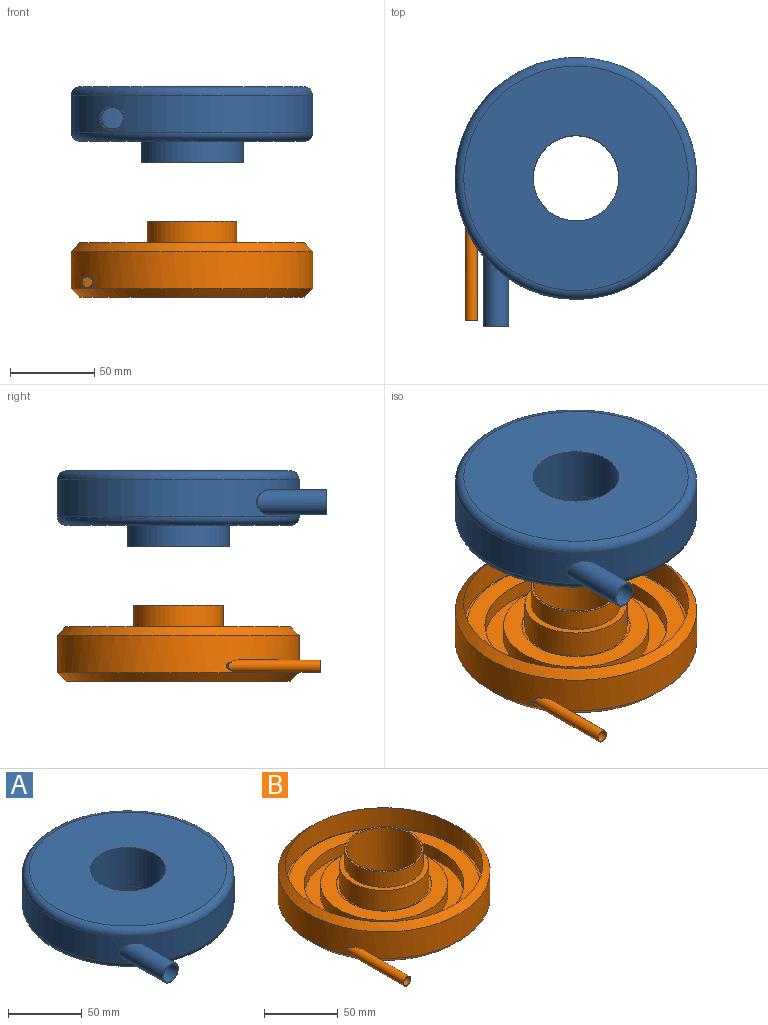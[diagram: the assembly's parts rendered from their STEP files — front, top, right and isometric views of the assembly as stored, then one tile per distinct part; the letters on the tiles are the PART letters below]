
ASSEMBLY  parts=2 mates=1
PART A: 19 faces, bbox 155.5x165.9x45 mm
  f0: cylinder r=71.84mm len=14.01mm, axis (0,0,1), area 32.2mm2, adj f12,f16
  f1: cylinder r=66.86mm len=133.73mm, axis (0,0,1), area 11339.2mm2, adj f9,f11,f12,f13,f14,f15
  f2: cylinder r=30.37mm len=60.74mm, axis (0,0,1), area 7668.5mm2, adj f3,f9
  f3: plane 60.74x60.74mm, normal (0,0,-1), area 665mm2, adj f2,f4
  f4: cylinder r=26.66mm len=53.32mm, axis (0,0,1), area 2127.3mm2, adj f3,f5
  f5: plane 53.32x53.32mm, normal (0,0,-1), area 206mm2, adj f4,f6
  f6: cylinder r=25.4mm len=50.8mm, axis (0,0,1), area 5156.7mm2, adj f5,f7
  f7: plane 133.53x133.53mm, normal (0,0,1), area 11976.3mm2, adj f6,f10
  f8: cylinder r=71.84mm len=143.69mm, axis (0,0,1), area 9765.1mm2, adj f10,f11,f17
  f9: plane 133.73x133.73mm, normal (0,0,-1), area 11148mm2, adj f1,f2
  f10: torus R=66.76mm, axis (0,0,-1), area 3509.5mm2, adj f7,f8
  f11: torus R=66.76mm, axis (0,0,-1), area 3466.8mm2, adj f1,f8
  f12: cylinder r=6.44mm len=19.3mm, axis (0,-1,0), area 280.1mm2, adj f0,f1
  f13: plane 14.95x13.64mm, normal (0,1,0), area 17.6mm2, adj f1,f14,f15
  f14: cylinder r=7.48mm len=14.95mm, axis (0,-1,0), area 316.2mm2, adj f1,f13
  f15: cylinder r=7.01mm len=14.01mm, axis (0,-1,0), area 294.9mm2, adj f1,f13
  f16: cylinder r=7.01mm len=41.12mm, axis (0,-1,0), area 1518mm2, adj f0,f18
  f17: cylinder r=7.48mm len=41.67mm, axis (0,-1,0), area 1622.3mm2, adj f8,f18
  f18: plane 14.95x14.95mm, normal (0,-1,0), area 21.3mm2, adj f16,f17
PART B: 36 faces, bbox 143.7x156.2x45 mm
  f0: plane 60.74x60.74mm, normal (0,0,1), area 665mm2, adj f1,f16
  f1: cylinder r=30.37mm len=60.74mm, axis (0,0,1), area 3205.6mm2, adj f0,f2
  f2: plane 64.4x64.4mm, normal (0,0,1), area 359.5mm2, adj f1,f3
  f3: cylinder r=32.2mm len=64.4mm, axis (0,0,1), area 203.9mm2, adj f2,f4
  f4: plane 86.14x86.14mm, normal (0,0,1), area 2570.7mm2, adj f3,f5
  f5: cylinder r=43.07mm len=86.14mm, axis (0,0,1), area 2605.8mm2, adj f4,f6
  f6: plane 108.33x108.33mm, normal (0,0,1), area 3388.9mm2, adj f5,f7
  f7: cylinder r=54.16mm len=108.33mm, axis (0,0,1), area 3277mm2, adj f6,f8
  f8: plane 130.07x130.07mm, normal (0,0,1), area 4071mm2, adj f7,f9
  f9: cylinder r=65.04mm len=130.07mm, axis (0,0,1), area 411.7mm2, adj f8,f10
  f10: plane 133.73x133.73mm, normal (0,0,1), area 757.9mm2, adj f9,f11
  f11: cylinder r=66.86mm len=133.73mm, axis (0,0,1), area 7014.8mm2, adj f10,f18
  f12: cylinder r=71.84mm len=143.69mm, axis (0,0,1), area 9910.1mm2, adj f18,f19,f21
  f13: plane 133.53x133.53mm, normal (0,0,-1), area 11084.5mm2, adj f17,f19
  f14: cylinder r=25.4mm len=50.8mm, axis (0,0,1), area 6372.8mm2, adj f15,f17
  f15: plane 53.32x53.32mm, normal (0,0,1), area 206mm2, adj f14,f16
  f16: cylinder r=26.66mm len=53.32mm, axis (0,0,1), area 2127.3mm2, adj f0,f15
  f17: cone r=30.48mm half-angle=45deg, axis (0,0,-1), area 1261.2mm2, adj f13,f14
  f18: cone r=66.76mm half-angle=45deg, axis (0,0,-1), area 3068mm2, adj f11,f12
  f19: cone r=71.84mm half-angle=45deg, axis (0,0,1), area 3128.3mm2, adj f12,f13
  f20: plane 7.29x7.29mm, normal (0,-1,0), area 4.8mm2, adj f21,f22
  f21: cylinder r=3.65mm len=55.73mm, axis (0,-1,0), area 1119.3mm2, adj f12,f20
  f22: cylinder r=3.43mm len=55.24mm, axis (0,-1,0), area 1052.3mm2, adj f20,f32
  f23: cylinder r=40.53mm len=81.06mm, axis (0,0,1), area 1971.6mm2, adj f24,f25
  f24: plane 81.06x81.06mm, normal (0,0,-1), area 2263.1mm2, adj f23,f26
  f25: plane 113.41x113.41mm, normal (0,0,-1), area 4940.7mm2, adj f23,f27
  f26: cylinder r=30.37mm len=60.74mm, axis (0,0,1), area 1648mm2, adj f24,f28
  f27: cylinder r=56.7mm len=113.41mm, axis (0,0,1), area 2758.4mm2, adj f25,f29
  f28: plane 133.73x133.73mm, normal (0,0,1), area 11148mm2, adj f26,f30
  f29: plane 133.73x133.73mm, normal (0,0,-1), area 3944.2mm2, adj f27,f30
  f30: cylinder r=66.86mm len=133.73mm, axis (0,0,1), area 3535.1mm2, adj f28,f29,f31,f33,f34,f35
  f31: cylinder r=3.11mm len=26.72mm, axis (0,-1,0), area 235.5mm2, adj f30,f32
  f32: cylinder r=71.84mm len=12.15mm, axis (0,0,1), area 13.5mm2, adj f22,f31
  f33: cylinder r=3.43mm len=7.14mm, axis (0,-1,0), area 49.7mm2, adj f30,f35
  f34: cylinder r=3.65mm len=7.54mm, axis (0,-1,0), area 55.9mm2, adj f30,f35
  f35: plane 7.29x3.54mm, normal (0,1,0), area 2.3mm2, adj f30,f33,f34
PLACE A t=(-62.35,31.68,4.27)mm
PLACE B t=(-62.35,31.68,-4.28)mm
MATE slider A.f0 <-> B.f1  axis (0,0,1) through (-62.35,31.68,63.42)mm
